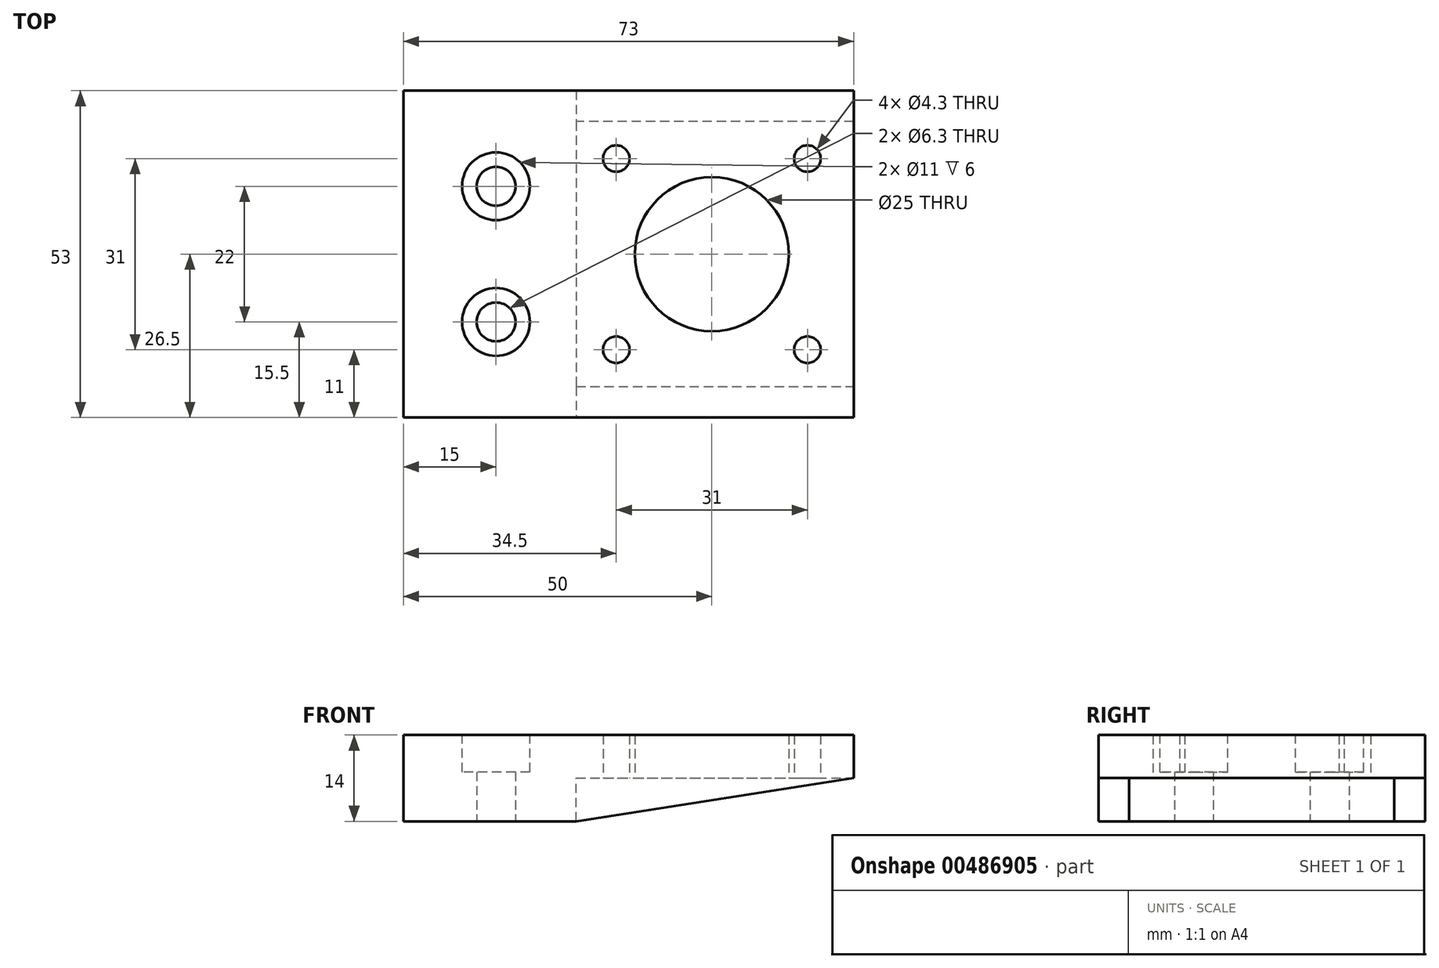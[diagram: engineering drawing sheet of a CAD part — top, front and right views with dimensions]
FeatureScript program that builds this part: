
annotation { "Feature Type Name" : "Feature", "Feature Type Description" : "" }
export const myFeature = defineFeature(function(context is Context, id is Id, definition is map)
    precondition{}
    {
        {
            var Q0;
            Q0=qCreatedBy(makeId("Top.planeOp"),FACE);
            var sketch = newSketch(context, id + "F0", { "sketchPlane" : qUnion([Q0])});
            skLineSegment(sketch, "E0.bottom", {"start": v(-36.5, 21.5) * mm, "end": v(36.5, 21.5) * mm});
            skLineSegment(sketch, "E0.top", {"start": v(-36.5, -21.5) * mm, "end": v(36.5, -21.5) * mm});
            skLineSegment(sketch, "E0.left", {"start": v(-36.5, 21.5) * mm, "end": v(-36.5, -21.5) * mm});
            skLineSegment(sketch, "E0.right", {"start": v(36.5, 21.5) * mm, "end": v(36.5, -21.5) * mm});
            skLineSegment(sketch, "E1.bottom", {"start": v(0, 0) * mm, "end": v(0, 0) * mm});
            skLineSegment(sketch, "E1.top", {"start": v(0, 21.5) * mm, "end": v(0, 21.5) * mm});
            skCircle(sketch, "E2", {"center": v(-21.5, 11) * mm, "radius": 3.15 * mm});
            skCircle(sketch, "E3", {"center": v(-21.5, -11) * mm, "radius": 3.15 * mm});
            skCircle(sketch, "E4", {"center": v(13.5, 0) * mm, "radius": 12.5 * mm});
            skCircle(sketch, "E5", {"center": v(29, 15.5) * mm, "radius": 2.15 * mm});
            skCircle(sketch, "E6", {"center": v(29, -15.5) * mm, "radius": 2.15 * mm});
            skCircle(sketch, "E7", {"center": v(-2, -15.5) * mm, "radius": 2.15 * mm});
            skCircle(sketch, "E8", {"center": v(-2, 15.5) * mm, "radius": 2.15 * mm});
            skSolve(sketch);
        }
        {
            var Q0;
            Q0 = qSketchRegion(id + "F0", true);
            extrude(context, id + "F1", {"entities" : qUnion([Q0]), "depth" : 20 * mm});
        }
        {
            var Q0;
            Q0=makeQuery(id+"F1.opExtrude","SWEPT_FACE",FACE,{"disambiguationData":[OSD([sQuery(id+"F0.wireOp",EDGE,"E0.top")])]});
            var sketch = newSketch(context, id + "F2", { "sketchPlane" : qUnion([Q0])});
            skLineSegment(sketch, "E9", {"start": v(-36.5, 14) * mm, "end": v(36.5, 14) * mm});
            skLineSegment(sketch, "E10", {"start": v(-8.5, 0) * mm, "end": v(-8.5, 7) * mm});
            skLineSegment(sketch, "E11", {"start": v(-8.5, 7) * mm, "end": v(36.5, 7) * mm});
            skLineSegment(sketch, "E12", {"start": v(-36.5, 14) * mm, "end": v(-36.5, 0) * mm});
            skLineSegment(sketch, "E13", {"start": v(-36.5, 0) * mm, "end": v(-8.5, 0) * mm});
            skLineSegment(sketch, "E14", {"start": v(-8.5, 0) * mm, "end": v(36.5, 0) * mm});
            skLineSegment(sketch, "E15", {"start": v(36.5, 0) * mm, "end": v(36.5, 7) * mm});
            skLineSegment(sketch, "E16", {"start": v(36.5, 14) * mm, "end": v(36.5, 20) * mm});
            skLineSegment(sketch, "E17", {"start": v(36.5, 20) * mm, "end": v(-36.5, 20) * mm});
            skLineSegment(sketch, "E18", {"start": v(-36.5, 20) * mm, "end": v(-36.5, 14) * mm});
            skSolve(sketch);
        }
        {
            var Q0;
            Q0=makeQuery(id+"F2.imprint","IMPRINT",FACE,{"disambiguationData":[TD([[makeQuery(id+"F2.imprint","IMPRINT",EDGE,{"derivedFrom":sQuery(id+"F2.wireOp",EDGE,"E9")}),1.0]])]});
            var Q1;
            Q1=makeQuery(id+"F2.imprint","IMPRINT",FACE,{"disambiguationData":[TD([[makeQuery(id+"F2.imprint","IMPRINT",EDGE,{"derivedFrom":sQuery(id+"F2.wireOp",EDGE,"E10")}),-1.0]])]});
            extrude(context, id + "F3", {"entities" : qUnion([Q0, Q1]), "operationType" : NewBodyOperationType.REMOVE, "endBound" : BoundingType.THROUGH_ALL, "oppositeDirection" : true, "depth" : 25 * mm});
        }
        {
            var Q0;
            Q0=makeQuery(id+"F3.boolean.opBoolean","COPY",FACE,{"derivedFrom":makeQuery(id+"F3.opExtrude","SWEPT_FACE",FACE,{"disambiguationData":[OSD([sQuery(id+"F2.wireOp",EDGE,"E9")])]})});
            var sketch = newSketch(context, id + "F4", { "sketchPlane" : qUnion([Q0])});
            skLineSegment(sketch, "E19", {"start": v(-36.5, -21.5) * mm, "end": v(36.5, -21.5) * mm});
            skLineSegment(sketch, "E20", {"start": v(36.5, -21.5) * mm, "end": v(36.5, -26.5) * mm});
            skLineSegment(sketch, "E21", {"start": v(36.5, -26.5) * mm, "end": v(-36.5, -26.5) * mm});
            skLineSegment(sketch, "E22", {"start": v(-36.5, -26.5) * mm, "end": v(-36.5, -21.5) * mm});
            skLineSegment(sketch, "E23.MirrorCS", {"start": v(-36.5, 26.5) * mm, "end": v(-36.5, 21.5) * mm});
            skLineSegment(sketch, "E24.MirrorCS", {"start": v(-36.5, 21.5) * mm, "end": v(36.5, 21.5) * mm});
            skLineSegment(sketch, "E25.MirrorCS", {"start": v(36.5, 26.5) * mm, "end": v(-36.5, 26.5) * mm});
            skLineSegment(sketch, "E26.MirrorCS", {"start": v(36.5, 21.5) * mm, "end": v(36.5, 26.5) * mm});
            skSolve(sketch);
        }
        {
            var Q0;
            Q0 = qSketchRegion(id + "F4", true);
            var Q1;
            Q1=makeQuery(id+"F1.opExtrude","CAP_FACE",FACE,{"disambiguationData":[OSD([sQuery(id+"F0.wireOp",EDGE,"E0.bottom"),sQuery(id+"F0.wireOp",EDGE,"E0.top"),sQuery(id+"F0.wireOp",EDGE,"E0.left"),sQuery(id+"F0.wireOp",EDGE,"E0.right"),sQuery(id+"F0.wireOp",EDGE,"E2"),sQuery(id+"F0.wireOp",EDGE,"E3"),sQuery(id+"F0.wireOp",EDGE,"E4"),sQuery(id+"F0.wireOp",EDGE,"E5"),sQuery(id+"F0.wireOp",EDGE,"E6"),sQuery(id+"F0.wireOp",EDGE,"E7"),sQuery(id+"F0.wireOp",EDGE,"E8")])],"isStart":true});
            extrude(context, id + "F5", {"entities" : qUnion([Q0]), "operationType" : NewBodyOperationType.ADD, "endBound" : BoundingType.UP_TO_SURFACE, "oppositeDirection" : true, "endBoundEntityFace" : qUnion([Q1]), "depth" : 25 * mm});
        }
        {
            var Q0;
            Q0=makeQuery(id+"F5.opExtrude","SWEPT_FACE",FACE,{"disambiguationData":[OSD([sQuery(id+"F4.wireOp",EDGE,"E21")])]});
            var sketch = newSketch(context, id + "F6", { "sketchPlane" : qUnion([Q0])});
            skLineSegment(sketch, "E27", {"start": v(-8.5, 0) * mm, "end": v(36.5, 7) * mm});
            skLineSegment(sketch, "E28", {"start": v(-8.5, 0) * mm, "end": v(36.5, 0) * mm});
            skLineSegment(sketch, "E29", {"start": v(36.5, 0) * mm, "end": v(36.5, 7) * mm});
            skSolve(sketch);
        }
        {
            var Q0;
            Q0 = qSketchRegion(id + "F6", true);
            extrude(context, id + "F7", {"entities" : qUnion([Q0]), "operationType" : NewBodyOperationType.REMOVE, "endBound" : BoundingType.THROUGH_ALL, "oppositeDirection" : true, "depth" : 25 * mm});
        }
        {
            var Q0;
            Q0=makeQuery(id+"F5.boolean.opBoolean","MERGE",FACE,{"derivedFrom":[makeQuery(id+"F3.boolean.opBoolean","COPY",FACE,{"derivedFrom":makeQuery(id+"F3.opExtrude","SWEPT_FACE",FACE,{"disambiguationData":[OSD([sQuery(id+"F2.wireOp",EDGE,"E9")])]})}),makeQuery(id+"F5.opExtrude","CAP_FACE",FACE,{"disambiguationData":[OSD([sQuery(id+"F4.wireOp",EDGE,"E19"),sQuery(id+"F4.wireOp",EDGE,"E20"),sQuery(id+"F4.wireOp",EDGE,"E21"),sQuery(id+"F4.wireOp",EDGE,"E22")])],"isStart":true}),makeQuery(id+"F5.opExtrude","CAP_FACE",FACE,{"disambiguationData":[OSD([sQuery(id+"F4.wireOp",EDGE,"E23.MirrorCS"),sQuery(id+"F4.wireOp",EDGE,"E24.MirrorCS"),sQuery(id+"F4.wireOp",EDGE,"E25.MirrorCS"),sQuery(id+"F4.wireOp",EDGE,"E26.MirrorCS")])],"isStart":true})]});
            var sketch = newSketch(context, id + "F8", { "sketchPlane" : qUnion([Q0])});
            skCircle(sketch, "E30", {"center": v(-21.5, 11) * mm, "radius": 5.5 * mm});
            skCircle(sketch, "E31", {"center": v(-21.5, -11) * mm, "radius": 5.5 * mm});
            skSolve(sketch);
        }
        {
            var Q0;
            Q0 = qSketchRegion(id + "F8", true);
            extrude(context, id + "F9", {"entities" : qUnion([Q0]), "operationType" : NewBodyOperationType.REMOVE, "oppositeDirection" : true, "depth" : 6 * mm});
        }
    });
